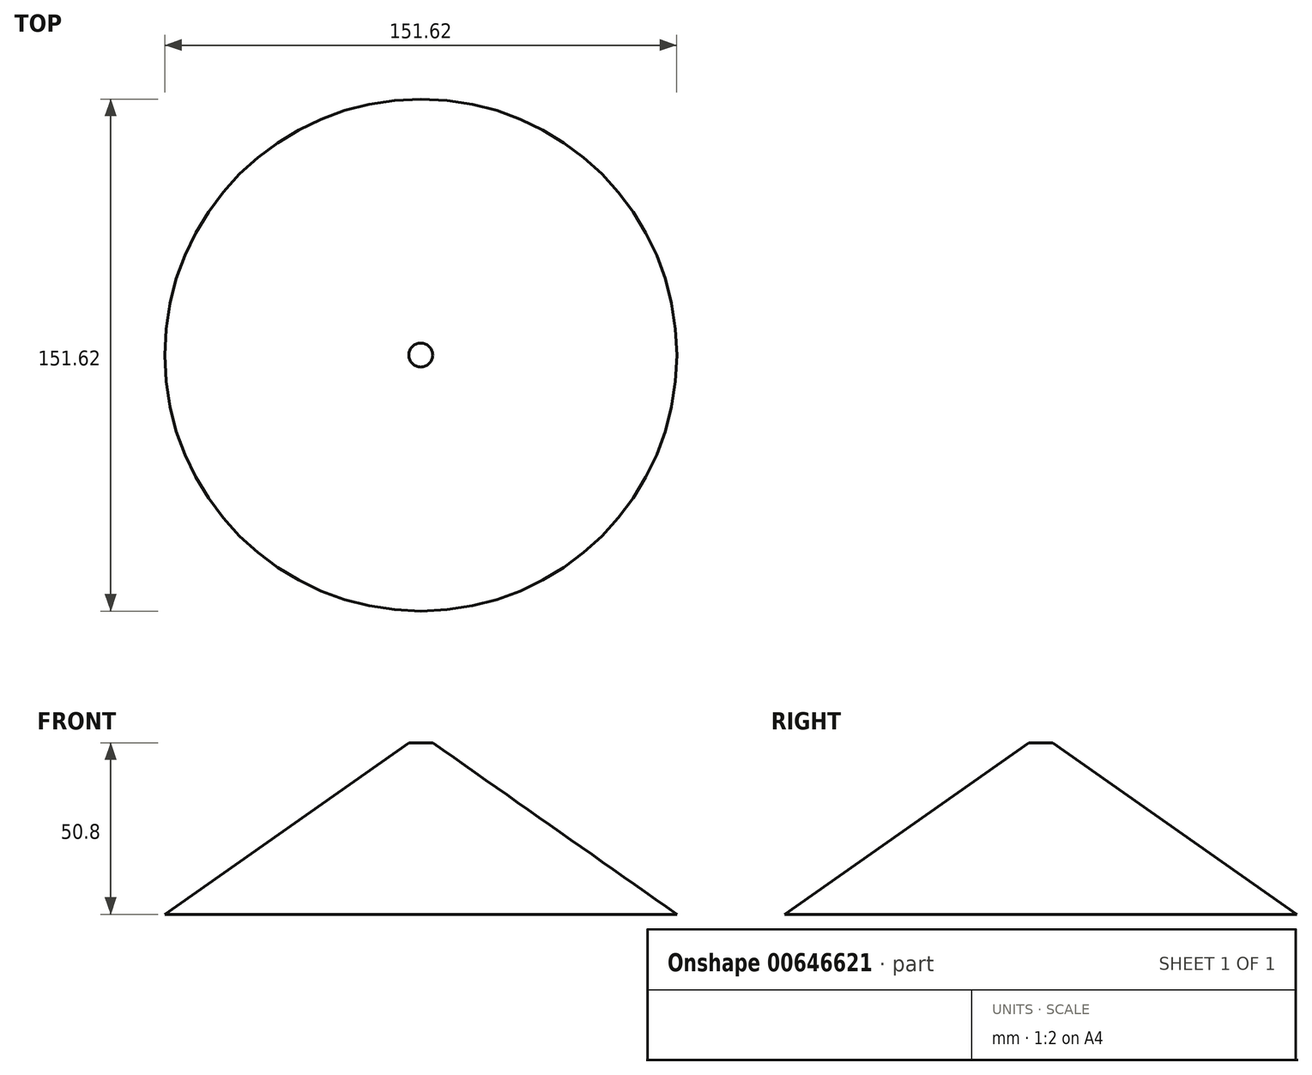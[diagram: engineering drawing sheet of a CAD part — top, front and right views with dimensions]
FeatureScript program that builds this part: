
annotation { "Feature Type Name" : "Feature", "Feature Type Description" : "" }
export const myFeature = defineFeature(function(context is Context, id is Id, definition is map)
    precondition{}
    {
        {
            var Q0;
            Q0=qCreatedBy(makeId("Top.planeOp"),FACE);
            var sketch = newSketch(context, id + "F0", { "sketchPlane" : qUnion([Q0])});
            skCircle(sketch, "E0", {"center": v(0, 0) * mm, "radius": 75.81 * mm});
            skSolve(sketch);
        }
        {
            var Q0;
            Q0=qCreatedBy(makeId("Top.planeOp"),FACE);
            cPlane(context, id + "F1", {"entities" : qUnion([Q0]), "cplaneType" : CPlaneType.OFFSET, "offset" : 50.8 * mm, "width" : 152.4 * mm, "height" : 152.4 * mm});
        }
        {
            var Q0;
            Q0=qCreatedBy(id+"F1.planeOp",FACE);
            var sketch = newSketch(context, id + "F2", { "sketchPlane" : qUnion([Q0])});
            skCircle(sketch, "E1", {"center": v(0, 0) * mm, "radius": 3.55 * mm});
            skSolve(sketch);
        }
        {
            var Q0;
            Q0=makeQuery(id+"F2.imprint","IMPRINT",FACE,{"disambiguationData":[TD([[makeQuery(id+"F2.imprint","IMPRINT",EDGE,{"derivedFrom":sQuery(id+"F2.wireOp",EDGE,"E1")}),1.0]])]});
            var Q1;
            Q1=makeQuery(id+"F0.imprint","IMPRINT",FACE,{"disambiguationData":[TD([[makeQuery(id+"F0.imprint","IMPRINT",EDGE,{"derivedFrom":sQuery(id+"F0.wireOp",EDGE,"E0")}),1.0]])]});
            loft(context, id + "F3", {"sheetProfilesArray" : [{ "sheetProfileEntities" : qUnion([Q0]) }, { "sheetProfileEntities" : qUnion([Q1]) }]});
        }
    });
